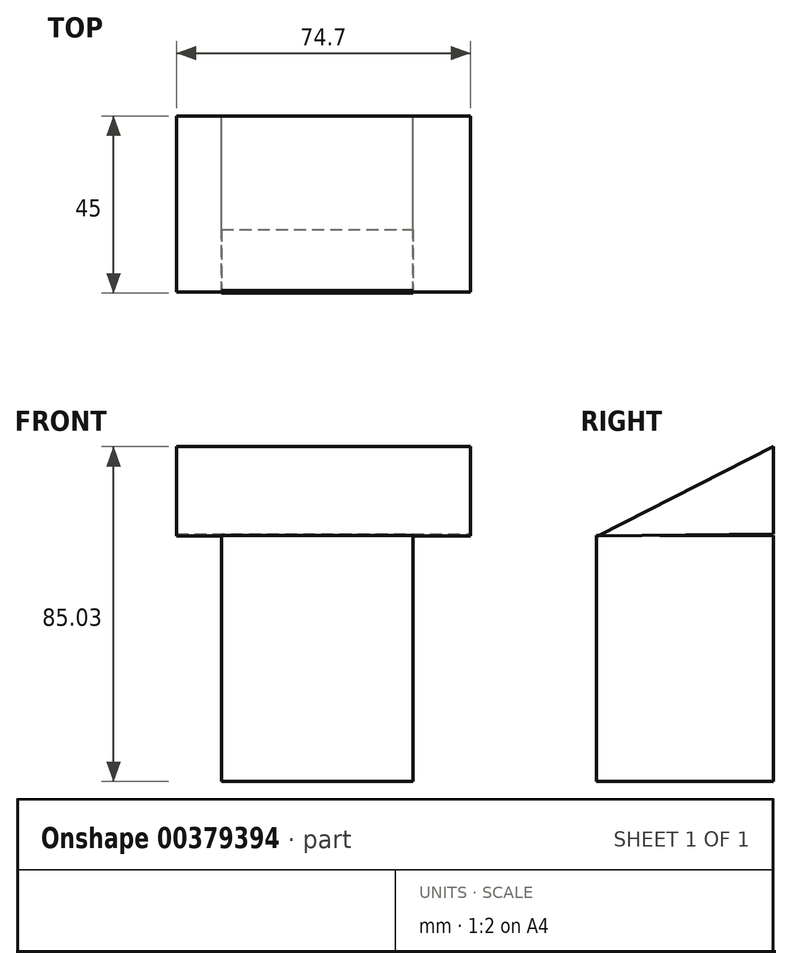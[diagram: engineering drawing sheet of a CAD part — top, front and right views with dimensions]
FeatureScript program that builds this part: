
annotation { "Feature Type Name" : "Feature", "Feature Type Description" : "" }
export const myFeature = defineFeature(function(context is Context, id is Id, definition is map)
    precondition{}
    {
        {
            var Q0;
            Q0=qCreatedBy(makeId("Front.planeOp"),FACE);
            var sketch = newSketch(context, id + "F0", { "sketchPlane" : qUnion([Q0])});
            skLineSegment(sketch, "E0.bottom", {"start": v(-63.24, 35.92) * mm, "end": v(-14.6, 35.92) * mm});
            skLineSegment(sketch, "E0.top", {"start": v(-63.24, -26.57) * mm, "end": v(-14.6, -26.57) * mm});
            skLineSegment(sketch, "E0.left", {"start": v(-63.24, 35.92) * mm, "end": v(-63.24, -26.57) * mm});
            skLineSegment(sketch, "E0.right", {"start": v(-14.6, 35.92) * mm, "end": v(-14.6, -26.57) * mm});
            skSolve(sketch);
        }
        {
            var Q0;
            Q0=makeQuery(id+"F0.imprint","IMPRINT",FACE,{"disambiguationData":[TD([[makeQuery(id+"F0.imprint","IMPRINT",EDGE,{"derivedFrom":sQuery(id+"F0.wireOp",EDGE,"E0.bottom")}),-1.0]])]});
            extrude(context, id + "F1", {"entities" : qUnion([Q0]), "depth" : 45 * mm});
        }
        {
            var Q0;
            Q0=qCreatedBy(makeId("Right.planeOp"),FACE);
            var sketch = newSketch(context, id + "F2", { "sketchPlane" : qUnion([Q0])});
            skLineSegment(sketch, "E1", {"start": v(-44.69, 35.75) * mm, "end": v(0, 58.46) * mm});
            skLineSegment(sketch, "E2", {"start": v(0, 58.46) * mm, "end": v(0, 36.23) * mm});
            skLineSegment(sketch, "E3", {"start": v(0, 36.23) * mm, "end": v(-44.69, 35.75) * mm});
            skSolve(sketch);
        }
        {
            var Q0;
            Q0=makeQuery(id+"F2.imprint","IMPRINT",FACE,{"disambiguationData":[TD([[makeQuery(id+"F2.imprint","IMPRINT",EDGE,{"derivedFrom":sQuery(id+"F2.wireOp",EDGE,"E1")}),-1.0]])]});
            extrude(context, id + "F3", {"entities" : qUnion([Q0]), "operationType" : NewBodyOperationType.ADD, "oppositeDirection" : true, "depth" : 74.7 * mm});
        }
    });
